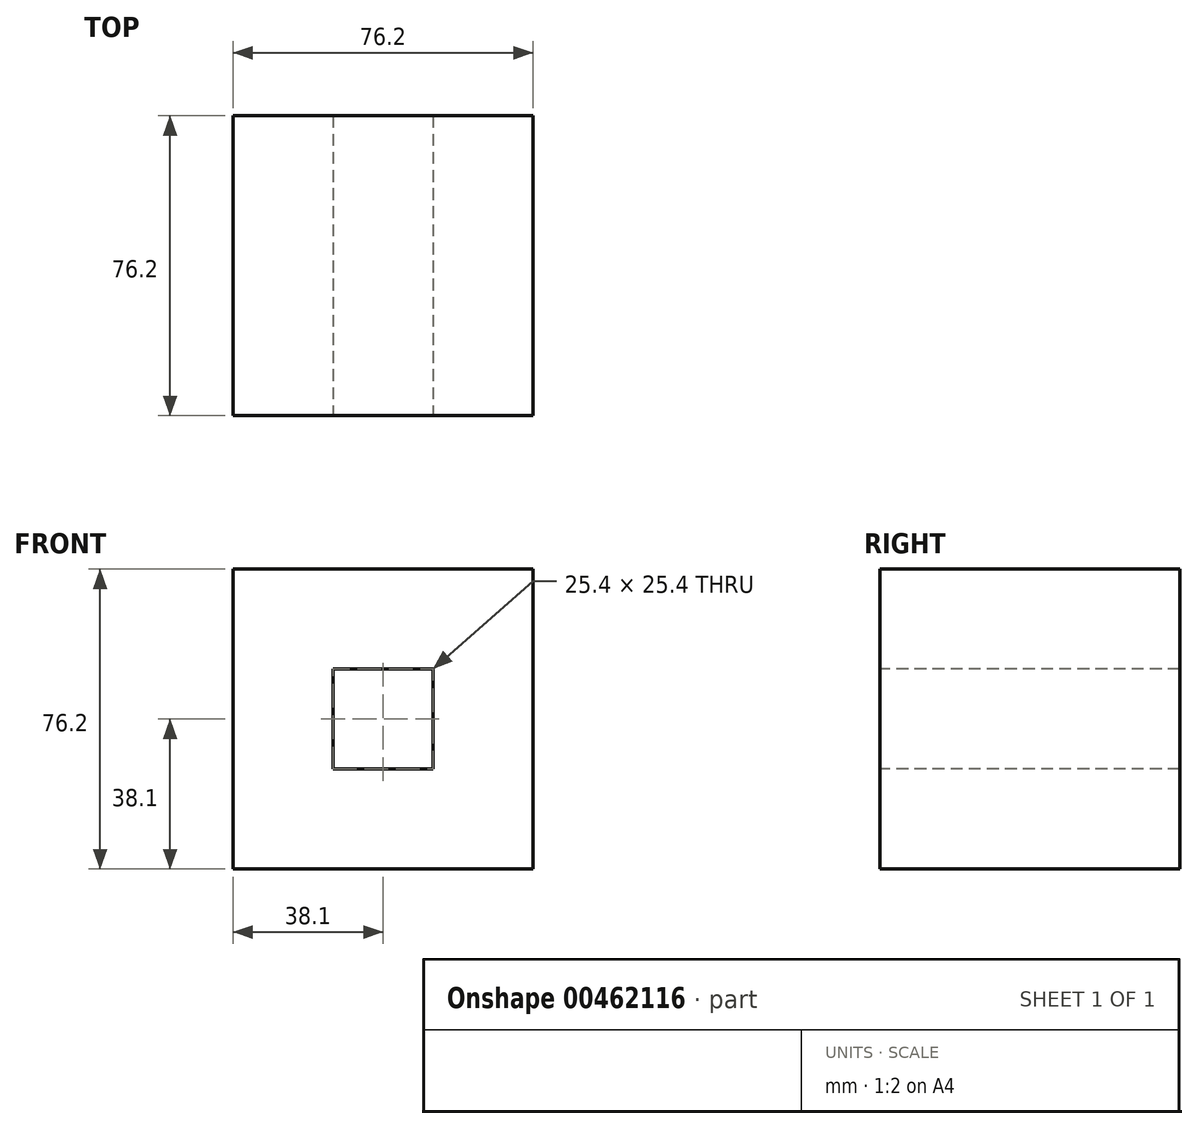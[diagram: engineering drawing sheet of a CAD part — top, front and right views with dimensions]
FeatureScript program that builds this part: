
annotation { "Feature Type Name" : "Feature", "Feature Type Description" : "" }
export const myFeature = defineFeature(function(context is Context, id is Id, definition is map)
    precondition{}
    {
        {
            var Q0;
            Q0=qCreatedBy(makeId("Front.planeOp"),FACE);
            var sketch = newSketch(context, id + "F0", { "sketchPlane" : qUnion([Q0])});
            skLineSegment(sketch, "E0.bottom", {"start": v(38.1, 38.1) * mm, "end": v(-38.1, 38.1) * mm});
            skLineSegment(sketch, "E0.top", {"start": v(38.1, -38.1) * mm, "end": v(-38.1, -38.1) * mm});
            skLineSegment(sketch, "E0.left", {"start": v(38.1, 38.1) * mm, "end": v(38.1, -38.1) * mm});
            skLineSegment(sketch, "E0.right", {"start": v(-38.1, 38.1) * mm, "end": v(-38.1, -38.1) * mm});
            skPoint(sketch, "E0.middle", {"position": v(0, 0) * mm});
            skSolve(sketch);
        }
        {
            var Q0;
            Q0 = qSketchRegion(id + "F0", true);
            extrude(context, id + "F1", {"entities" : qUnion([Q0]), "endBound" : BoundingType.SYMMETRIC, "depth" : 76.2 * mm});
        }
        {
            var Q0;
            Q0=makeQuery(id+"F1.opExtrude","CAP_FACE",FACE,{"disambiguationData":[OSD([sQuery(id+"F0.wireOp",EDGE,"E0.bottom"),sQuery(id+"F0.wireOp",EDGE,"E0.top"),sQuery(id+"F0.wireOp",EDGE,"E0.left"),sQuery(id+"F0.wireOp",EDGE,"E0.right")])],"isStart":false});
            var sketch = newSketch(context, id + "F2", { "sketchPlane" : qUnion([Q0])});
            skLineSegment(sketch, "E1.bottom", {"start": v(12.7, 12.7) * mm, "end": v(-12.7, 12.7) * mm});
            skLineSegment(sketch, "E1.top", {"start": v(12.7, -12.7) * mm, "end": v(-12.7, -12.7) * mm});
            skLineSegment(sketch, "E1.left", {"start": v(12.7, 12.7) * mm, "end": v(12.7, -12.7) * mm});
            skLineSegment(sketch, "E1.right", {"start": v(-12.7, 12.7) * mm, "end": v(-12.7, -12.7) * mm});
            skPoint(sketch, "E1.middle", {"position": v(0, 0) * mm});
            skSolve(sketch);
        }
        {
            var Q0;
            Q0=makeQuery(id+"F2.imprint","IMPRINT",FACE,{"disambiguationData":[TD([[makeQuery(id+"F2.imprint","IMPRINT",EDGE,{"derivedFrom":sQuery(id+"F2.wireOp",EDGE,"E1.bottom")}),1.0]])]});
            var sketch = newSketch(context, id + "F3", { "sketchPlane" : qUnion([Q0])});
            skLineSegment(sketch, "E2.bottom", {"start": v(12.7, 12.7) * mm, "end": v(-12.7, 12.7) * mm});
            skLineSegment(sketch, "E2.top", {"start": v(12.7, -12.7) * mm, "end": v(-12.7, -12.7) * mm});
            skLineSegment(sketch, "E2.left", {"start": v(12.7, 12.7) * mm, "end": v(12.7, -12.7) * mm});
            skLineSegment(sketch, "E2.right", {"start": v(-12.7, 12.7) * mm, "end": v(-12.7, -12.7) * mm});
            skPoint(sketch, "E2.middle", {"position": v(0, 0) * mm});
            skSolve(sketch);
        }
        {
            var Q0;
            Q0 = qSketchRegion(id + "F3", true);
            extrude(context, id + "F4", {"entities" : qUnion([Q0]), "operationType" : NewBodyOperationType.REMOVE, "endBound" : BoundingType.THROUGH_ALL, "oppositeDirection" : true, "depth" : 25.4 * mm});
        }
    });
